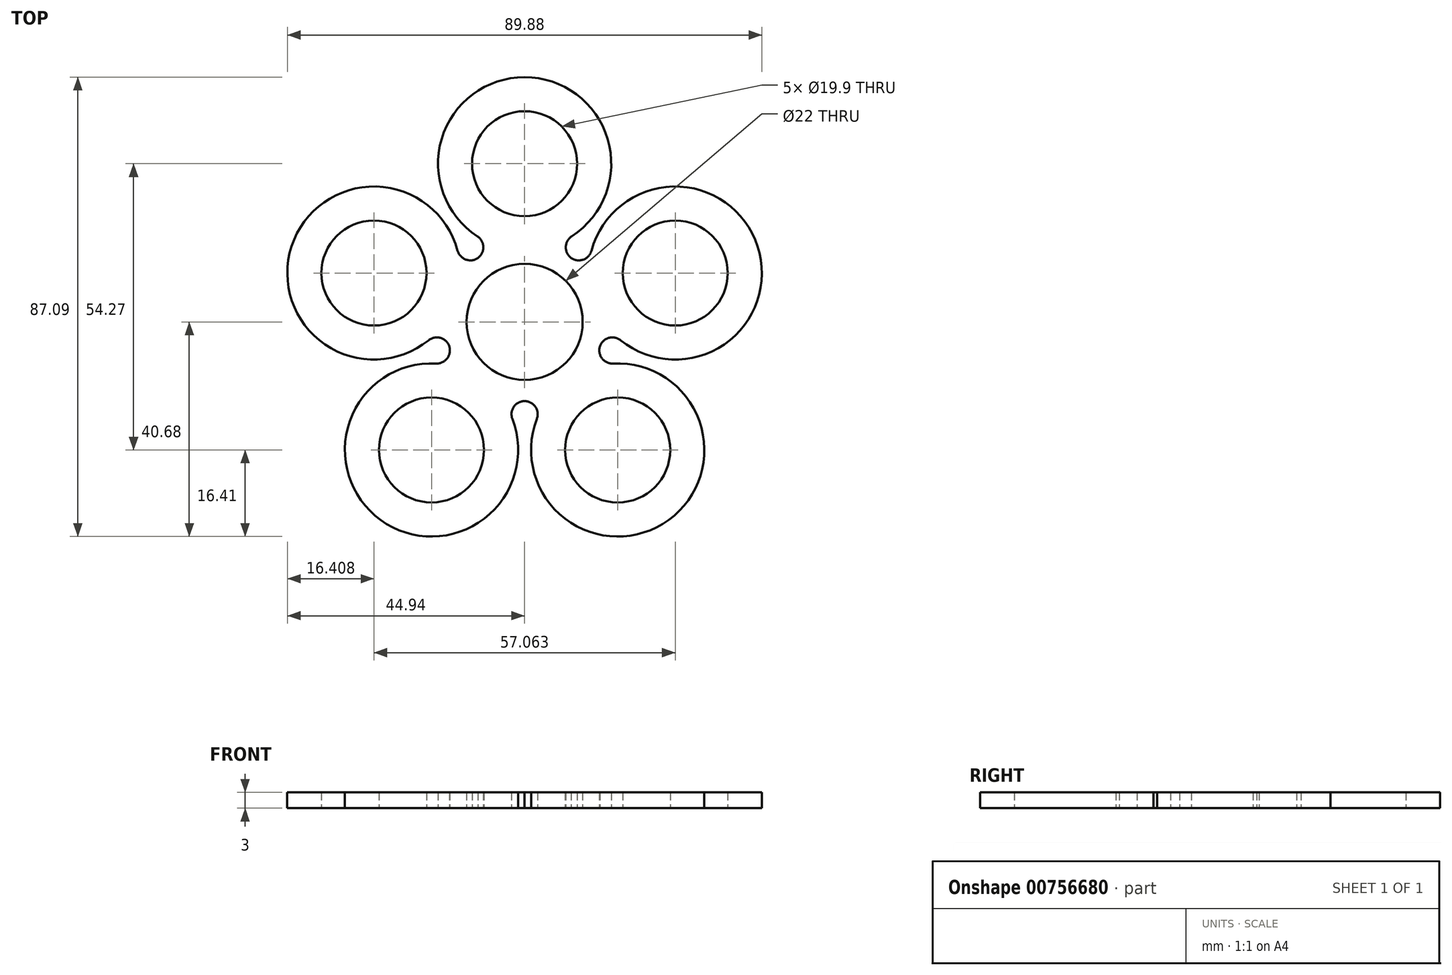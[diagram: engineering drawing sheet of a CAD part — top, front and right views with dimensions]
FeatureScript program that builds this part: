
annotation { "Feature Type Name" : "Feature", "Feature Type Description" : "" }
export const myFeature = defineFeature(function(context is Context, id is Id, definition is map)
    precondition{}
    {
        {
            var Q0;
            Q0=qCreatedBy(makeId("Top.planeOp"),FACE);
            var sketch = newSketch(context, id + "F0", { "sketchPlane" : qUnion([Q0])});
            skCircle(sketch, "E0", {"center": v(0, 0) * mm, "radius": 11 * mm});
            skCircle(sketch, "E1", {"center": v(0, 30) * mm, "radius": 9.95 * mm});
            skArc(sketch, "E2", {"start": v(8.94, 16.24) * mm, "mid": v(0, 46.4) * mm, "end": v(-8.94, 16.24) * mm});
            skArc(sketch, "E3.1.0", {"start": v(-12.68, 13.52) * mm, "mid": v(-44.14, 14.34) * mm, "end": v(-18.2, -3.49) * mm});
            skCircle(sketch, "E3.1.1", {"center": v(-28.53, 9.27) * mm, "radius": 9.95 * mm});
            skArc(sketch, "E3.2.0", {"start": v(-16.78, -7.88) * mm, "mid": v(-27.28, -37.55) * mm, "end": v(-2.31, -18.4) * mm});
            skCircle(sketch, "E3.2.1", {"center": v(-17.63, -24.27) * mm, "radius": 9.95 * mm});
            skArc(sketch, "E3.3.0", {"start": v(2.31, -18.4) * mm, "mid": v(27.28, -37.55) * mm, "end": v(16.78, -7.88) * mm});
            skCircle(sketch, "E3.3.1", {"center": v(17.63, -24.27) * mm, "radius": 9.95 * mm});
            skArc(sketch, "E3.4.0", {"start": v(18.2, -3.49) * mm, "mid": v(44.14, 14.34) * mm, "end": v(12.68, 13.52) * mm});
            skCircle(sketch, "E3.4.1", {"center": v(28.53, 9.27) * mm, "radius": 9.95 * mm});
            skPoint(sketch, "E4.visualSharp", {"position": v(-4.65, 14.26) * mm});
            skArc(sketch, "E4.filletArc", {"start": v(-8.83, 12.12) * mm, "mid": v(-7.8, 14.21) * mm, "end": v(-8.94, 16.24) * mm});
            skPoint(sketch, "E5.visualSharp", {"position": v(-12.13, 8.83) * mm});
            skArc(sketch, "E5.filletArc", {"start": v(-12.68, 13.52) * mm, "mid": v(-11.1, 11.81) * mm, "end": v(-8.8, 12.15) * mm});
            skPoint(sketch, "E6.visualSharp", {"position": v(4.65, 14.26) * mm});
            skArc(sketch, "E6.filletArc", {"start": v(8.94, 16.24) * mm, "mid": v(7.8, 14.21) * mm, "end": v(8.83, 12.12) * mm});
            skPoint(sketch, "E7.visualSharp", {"position": v(12.13, 8.83) * mm});
            skArc(sketch, "E7.filletArc", {"start": v(8.8, 12.15) * mm, "mid": v(11.1, 11.81) * mm, "end": v(12.68, 13.52) * mm});
            skPoint(sketch, "E8.visualSharp", {"position": v(15, -0.01) * mm});
            skArc(sketch, "E8.filletArc", {"start": v(18.2, -3.49) * mm, "mid": v(15.93, -3.03) * mm, "end": v(14.26, -4.65) * mm});
            skPoint(sketch, "E9.visualSharp", {"position": v(12.14, -8.8) * mm});
            skArc(sketch, "E9.filletArc", {"start": v(14.27, -4.62) * mm, "mid": v(14.67, -6.9) * mm, "end": v(16.78, -7.88) * mm});
            skPoint(sketch, "E10.visualSharp", {"position": v(4.62, -14.27) * mm});
            skArc(sketch, "E10.filletArc", {"start": v(2.31, -18.4) * mm, "mid": v(2.04, -16.08) * mm, "end": v(-0.02, -15) * mm});
            skPoint(sketch, "E11.visualSharp", {"position": v(-4.62, -14.27) * mm});
            skArc(sketch, "E11.filletArc", {"start": v(0.02, -15) * mm, "mid": v(-2.04, -16.08) * mm, "end": v(-2.31, -18.4) * mm});
            skPoint(sketch, "E12.visualSharp", {"position": v(-12.14, -8.8) * mm});
            skArc(sketch, "E12.filletArc", {"start": v(-16.78, -7.88) * mm, "mid": v(-14.67, -6.9) * mm, "end": v(-14.27, -4.62) * mm});
            skPoint(sketch, "E13.visualSharp", {"position": v(-15, -0.01) * mm});
            skArc(sketch, "E13.filletArc", {"start": v(-14.26, -4.65) * mm, "mid": v(-15.93, -3.03) * mm, "end": v(-18.2, -3.49) * mm});
            skSolve(sketch);
        }
        {
            var Q0;
            Q0=makeQuery(id+"F0.imprint","IMPRINT",FACE,{"disambiguationData":[TD([[makeQuery(id+"F0.imprint","IMPRINT",EDGE,{"derivedFrom":sQuery(id+"F0.wireOp",EDGE,"E0")}),-1.0]])]});
            extrude(context, id + "F1", {"entities" : qUnion([Q0]), "depth" : 3 * mm, "offsetDistance" : 25 * mm});
        }
    });
